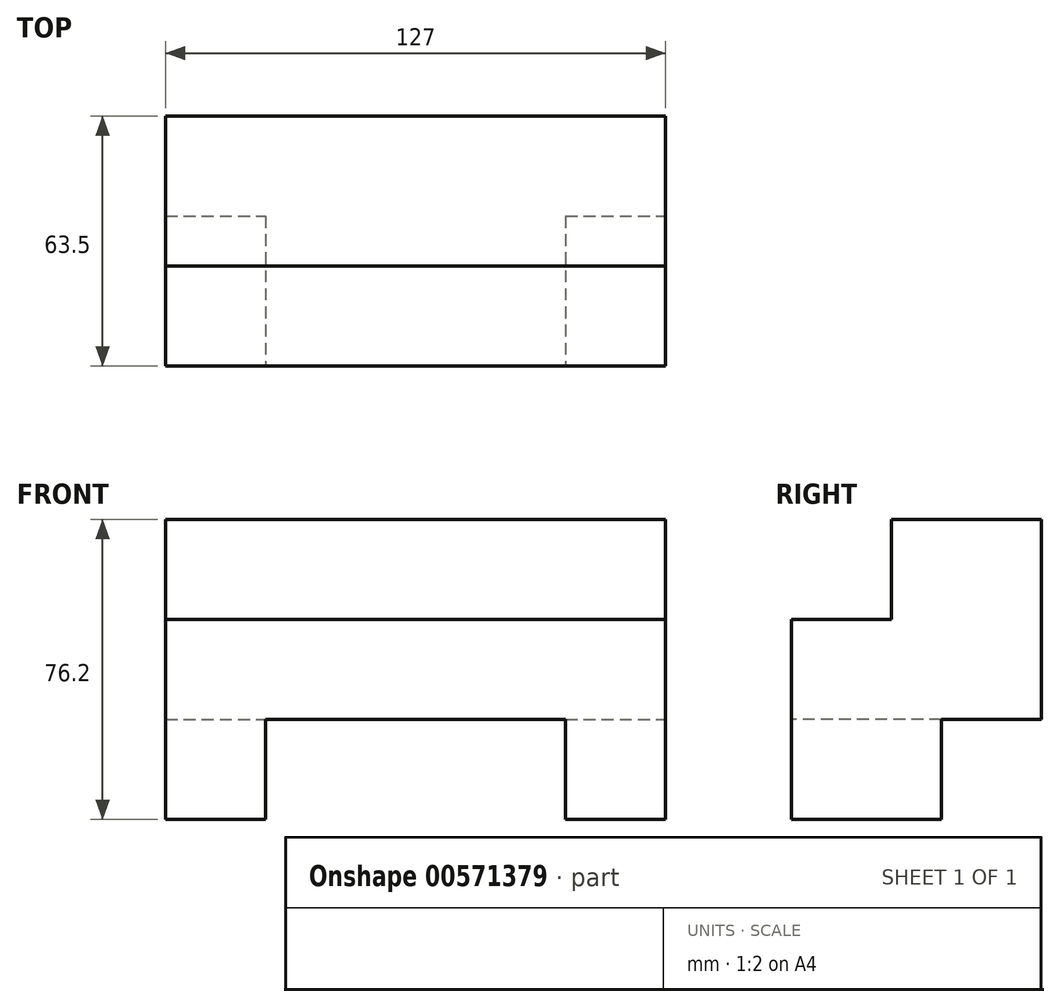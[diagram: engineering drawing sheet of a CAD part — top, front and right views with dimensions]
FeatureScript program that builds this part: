
annotation { "Feature Type Name" : "Feature", "Feature Type Description" : "" }
export const myFeature = defineFeature(function(context is Context, id is Id, definition is map)
    precondition{}
    {
        {
            var Q0;
            Q0=qCreatedBy(makeId("Front.planeOp"),FACE);
            var sketch = newSketch(context, id + "F0", { "sketchPlane" : qUnion([Q0])});
            skLineSegment(sketch, "E0.bottom", {"start": v(-86.03, 18.6) * mm, "end": v(40.97, 18.6) * mm});
            skLineSegment(sketch, "E0.top", {"start": v(-86.03, -57.6) * mm, "end": v(40.97, -57.6) * mm});
            skLineSegment(sketch, "E0.left", {"start": v(-86.03, 18.6) * mm, "end": v(-86.03, -57.6) * mm});
            skLineSegment(sketch, "E0.right", {"start": v(40.97, 18.6) * mm, "end": v(40.97, -57.6) * mm});
            skSolve(sketch);
        }
        {
            var Q0;
            Q0 = qSketchRegion(id + "F0", true);
            extrude(context, id + "F1", {"entities" : qUnion([Q0]), "depth" : 63.5 * mm, "offsetDistance" : 25.4 * mm});
        }
        {
            var Q0;
            Q0=makeQuery(id+"F1.opExtrude","CAP_FACE",FACE,{"disambiguationData":[OSD([sQuery(id+"F0.wireOp",EDGE,"E0.bottom"),sQuery(id+"F0.wireOp",EDGE,"E0.top"),sQuery(id+"F0.wireOp",EDGE,"E0.left"),sQuery(id+"F0.wireOp",EDGE,"E0.right")])],"isStart":false});
            var sketch = newSketch(context, id + "F2", { "sketchPlane" : qUnion([Q0])});
            skLineSegment(sketch, "E1", {"start": v(-86.03, -57.6) * mm, "end": v(-60.63, -57.6) * mm});
            skLineSegment(sketch, "E2", {"start": v(-60.63, -57.6) * mm, "end": v(-60.63, -32.2) * mm});
            skLineSegment(sketch, "E3", {"start": v(40.97, -57.6) * mm, "end": v(15.57, -57.6) * mm});
            skLineSegment(sketch, "E4", {"start": v(15.57, -57.6) * mm, "end": v(15.57, -32.2) * mm});
            skLineSegment(sketch, "E5", {"start": v(15.57, -32.2) * mm, "end": v(-60.63, -32.2) * mm});
            skLineSegment(sketch, "E6", {"start": v(-60.63, -57.6) * mm, "end": v(15.57, -57.6) * mm});
            skSolve(sketch);
        }
        {
            var Q0;
            Q0=makeQuery(id+"F2.imprint","IMPRINT",FACE,{"disambiguationData":[TD([[makeQuery(id+"F2.imprint","IMPRINT",EDGE,{"derivedFrom":sQuery(id+"F2.wireOp",EDGE,"E2")}),-1.0]])]});
            extrude(context, id + "F3", {"entities" : qUnion([Q0]), "operationType" : NewBodyOperationType.REMOVE, "endBound" : BoundingType.THROUGH_ALL, "oppositeDirection" : true, "depth" : 25.4 * mm, "offsetDistance" : 25.4 * mm});
        }
        {
            var Q0;
            Q0=makeQuery(id+"F1.opExtrude","SWEPT_FACE",FACE,{"disambiguationData":[OSD([sQuery(id+"F0.wireOp",EDGE,"E0.right")])]});
            var sketch = newSketch(context, id + "F4", { "sketchPlane" : qUnion([Q0])});
            skLineSegment(sketch, "E7", {"start": v(-63.5, 18.6) * mm, "end": v(-38.1, 18.6) * mm});
            skLineSegment(sketch, "E8", {"start": v(-38.1, 18.6) * mm, "end": v(-38.1, -6.8) * mm});
            skLineSegment(sketch, "E9", {"start": v(-38.1, -6.8) * mm, "end": v(-63.5, -6.8) * mm});
            skLineSegment(sketch, "E10", {"start": v(-63.5, -6.8) * mm, "end": v(-63.5, 18.6) * mm});
            skLineSegment(sketch, "E11", {"start": v(0, -57.6) * mm, "end": v(0, -32.2) * mm});
            skLineSegment(sketch, "E12", {"start": v(0, -32.2) * mm, "end": v(-25.4, -32.2) * mm});
            skLineSegment(sketch, "E13", {"start": v(-25.4, -32.2) * mm, "end": v(-25.4, -57.6) * mm});
            skLineSegment(sketch, "E14", {"start": v(-25.4, -57.6) * mm, "end": v(0, -57.6) * mm});
            skSolve(sketch);
        }
        {
            var Q0;
            Q0=makeQuery(id+"F4.imprint","IMPRINT",FACE,{"disambiguationData":[TD([[makeQuery(id+"F4.imprint","IMPRINT",EDGE,{"derivedFrom":sQuery(id+"F4.wireOp",EDGE,"E11")}),-1.0]])]});
            var Q1;
            Q1=makeQuery(id+"F4.imprint","IMPRINT",FACE,{"disambiguationData":[TD([[makeQuery(id+"F4.imprint","IMPRINT",EDGE,{"derivedFrom":sQuery(id+"F4.wireOp",EDGE,"E7")}),-1.0]])]});
            extrude(context, id + "F5", {"entities" : qUnion([Q0, Q1]), "operationType" : NewBodyOperationType.REMOVE, "endBound" : BoundingType.THROUGH_ALL, "oppositeDirection" : true, "depth" : 25.4 * mm, "offsetDistance" : 25.4 * mm});
        }
    });
